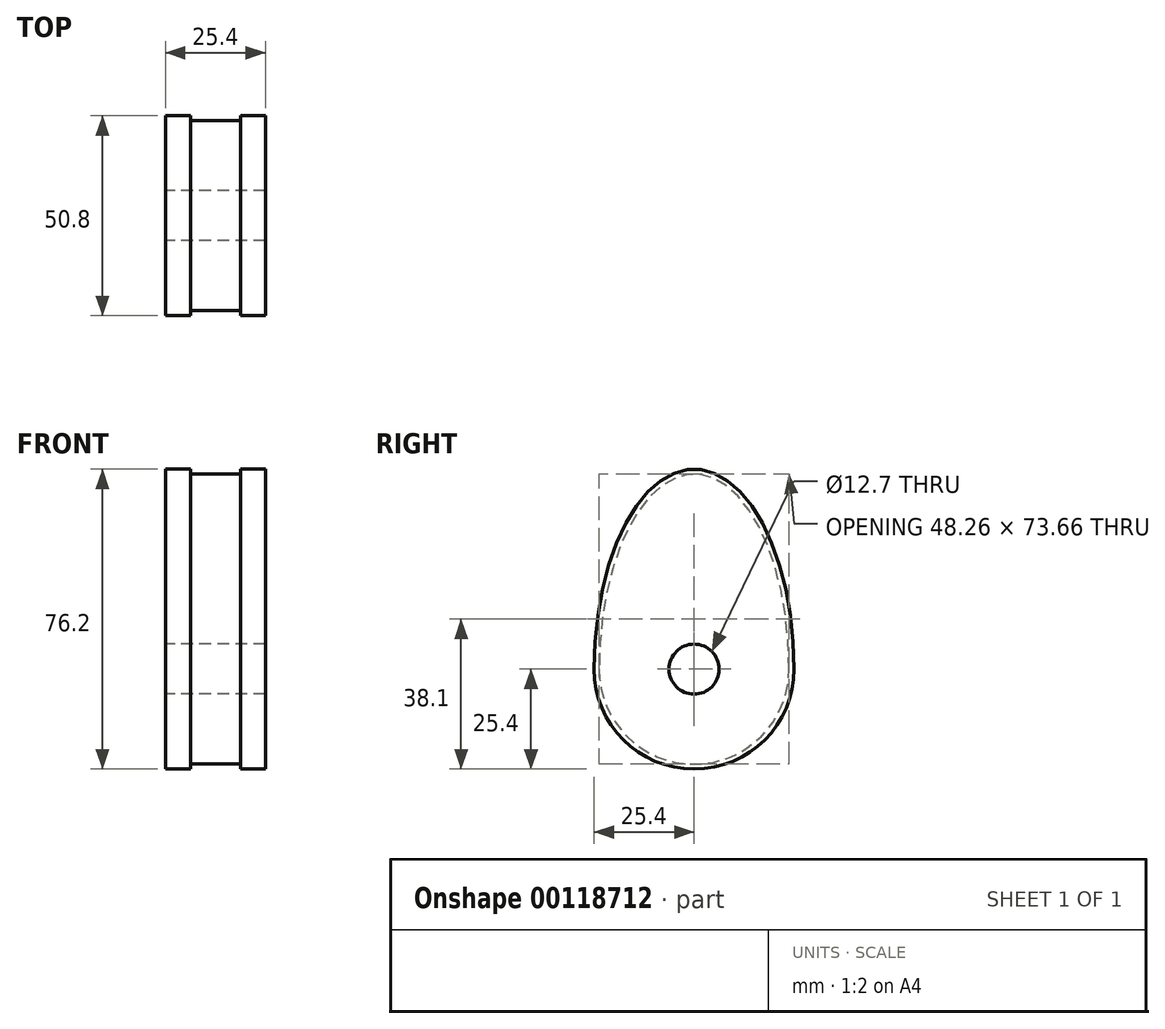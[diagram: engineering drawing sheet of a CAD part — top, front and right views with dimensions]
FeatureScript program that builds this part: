
annotation { "Feature Type Name" : "Feature", "Feature Type Description" : "" }
export const myFeature = defineFeature(function(context is Context, id is Id, definition is map)
    precondition{}
    {
        {
            var Q0;
            Q0=qCreatedBy(makeId("Right.planeOp"),FACE);
            var sketch = newSketch(context, id + "F0", { "sketchPlane" : qUnion([Q0])});
            skCircle(sketch, "E0", {"center": v(0, 0) * mm, "radius": 25.4 * mm});
            skEllipticalArc(sketch, "E1", {});
            skPoint(sketch, "E2", {"position": v(0, 25.4) * mm});
            skPoint(sketch, "E3", {"position": v(0, 50.8) * mm});
            const initialGuessF0  = {"E1": [0, 0, 0, 1, 0.0508, 0.0254, 4.71238898038469, 1.5707963267948966]};
            skSetInitialGuess(sketch, initialGuessF0);
            skSolve(sketch);
        }
        {
            var Q0;
            Q0 = qSketchRegion(id + "F0", true);
            extrude(context, id + "F1", {"entities" : qUnion([Q0]), "endBound" : BoundingType.SYMMETRIC, "depth" : 25.4 * mm});
        }
        {
            var Q0;
            Q0=qCreatedBy(makeId("Right.planeOp"),FACE);
            var sketch = newSketch(context, id + "F2", { "sketchPlane" : qUnion([Q0])});
            skEllipticalArc(sketch, "E4.0", {});
            skArc(sketch, "E5.0", {"start": v(-25.4, 0) * mm, "mid": v(0, -25.4) * mm, "end": v(25.4, 0) * mm});
            const initialGuessF2  = {"E4.0": [0, 0, 0, 1, 0.0508, 0.0254, 4.71238898038469, 1.5707963267948966]};
            skSetInitialGuess(sketch, initialGuessF2);
            skSolve(sketch);
        }
        {
            var Q0;
            Q0 = qSketchRegion(id + "F2", true);
            extrude(context, id + "F3", {"entities" : qUnion([Q0]), "operationType" : NewBodyOperationType.REMOVE, "endBound" : BoundingType.SYMMETRIC, "oppositeDirection" : true, "depth" : 12.7 * mm});
        }
        {
            var Q0;
            Q0=qCreatedBy(makeId("Right.planeOp"),FACE);
            var sketch = newSketch(context, id + "F4", { "sketchPlane" : qUnion([Q0])});
            skCircle(sketch, "E6", {"center": v(0, 0) * mm, "radius": 24.13 * mm});
            skEllipticalArc(sketch, "E7", {});
            skPoint(sketch, "E8", {"position": v(0, 24.13) * mm});
            skPoint(sketch, "E9", {"position": v(0, 49.53) * mm});
            const initialGuessF4  = {"E7": [0, 0, 0, 1, 0.04953, 0.02413, 4.71238898038469, 1.5707963267948966]};
            skSetInitialGuess(sketch, initialGuessF4);
            skSolve(sketch);
        }
        {
            var Q0;
            Q0 = qSketchRegion(id + "F4", true);
            extrude(context, id + "F5", {"entities" : qUnion([Q0]), "operationType" : NewBodyOperationType.ADD, "endBound" : BoundingType.SYMMETRIC, "depth" : 15.24 * mm});
        }
        {
            var Q0;
            Q0=makeQuery(id+"F1.opExtrude","CAP_FACE",FACE,{"disambiguationData":[OSD([sQuery(id+"F0.wireOp",EDGE,"E0"),sQuery(id+"F0.wireOp",EDGE,"E1")])],"isStart":true});
            var sketch = newSketch(context, id + "F6", { "sketchPlane" : qUnion([Q0])});
            skCircle(sketch, "E10", {"center": v(0, 0) * mm, "radius": 6.35 * mm});
            skSolve(sketch);
        }
        {
            var Q0;
            Q0=makeQuery(id+"F6.imprint","IMPRINT",FACE,{"disambiguationData":[TD([[makeQuery(id+"F6.imprint","IMPRINT",EDGE,{"derivedFrom":sQuery(id+"F6.wireOp",EDGE,"E10")}),1.0]])]});
            extrude(context, id + "F7", {"entities" : qUnion([Q0]), "operationType" : NewBodyOperationType.REMOVE, "endBound" : BoundingType.THROUGH_ALL, "oppositeDirection" : true, "depth" : 25.4 * mm});
        }
    });
